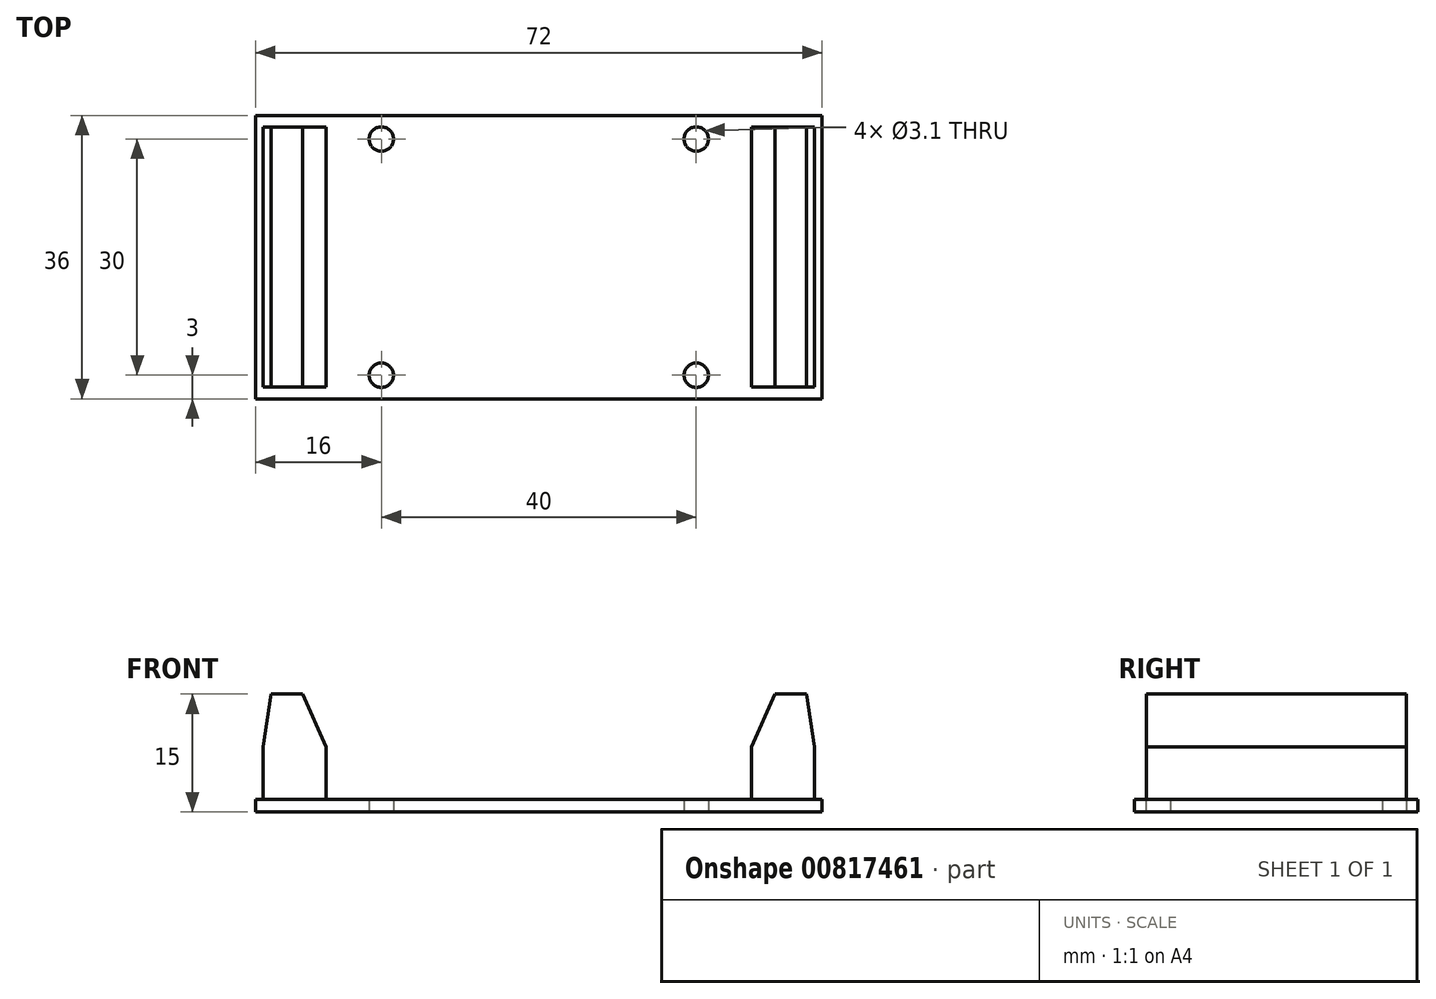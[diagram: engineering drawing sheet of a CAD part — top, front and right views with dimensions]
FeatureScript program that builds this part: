
annotation { "Feature Type Name" : "Feature", "Feature Type Description" : "" }
export const myFeature = defineFeature(function(context is Context, id is Id, definition is map)
    precondition{}
    {
        {
            var Q0;
            Q0=qCreatedBy(makeId("Top.planeOp"),FACE);
            var sketch = newSketch(context, id + "F0", { "sketchPlane" : qUnion([Q0])});
            skLineSegment(sketch, "E0.bottom", {"start": v(36, 18) * mm, "end": v(-36, 18) * mm});
            skLineSegment(sketch, "E0.top", {"start": v(36, -18) * mm, "end": v(-36, -18) * mm});
            skLineSegment(sketch, "E0.left", {"start": v(36, 18) * mm, "end": v(36, -18) * mm});
            skLineSegment(sketch, "E0.right", {"start": v(-36, 18) * mm, "end": v(-36, -18) * mm});
            skPoint(sketch, "E0.middle", {"position": v(0, 0) * mm});
            skLineSegment(sketch, "E1.bottom", {"start": v(20, 15) * mm, "end": v(-20, 15) * mm, "construction": true});
            skLineSegment(sketch, "E1.top", {"start": v(20, -15) * mm, "end": v(-20, -15) * mm, "construction": true});
            skLineSegment(sketch, "E1.left", {"start": v(20, 15) * mm, "end": v(20, -15) * mm, "construction": true});
            skLineSegment(sketch, "E1.right", {"start": v(-20, 15) * mm, "end": v(-20, -15) * mm, "construction": true});
            skCircle(sketch, "E2", {"center": v(-20, 15) * mm, "radius": 1.55 * mm});
            skCircle(sketch, "E3", {"center": v(20, 15) * mm, "radius": 1.55 * mm});
            skCircle(sketch, "E4", {"center": v(20, -15) * mm, "radius": 1.55 * mm});
            skCircle(sketch, "E5", {"center": v(-20, -15) * mm, "radius": 1.55 * mm});
            skSolve(sketch);
        }
        {
            var Q0;
            Q0=makeQuery(id+"F0.imprint","IMPRINT",FACE,{"disambiguationData":[TD([[makeQuery(id+"F0.imprint","IMPRINT",EDGE,{"derivedFrom":sQuery(id+"F0.wireOp",EDGE,"E0.bottom")}),1.0]])]});
            extrude(context, id + "F1", {"entities" : qUnion([Q0]), "depth" : 1.6 * mm, "offsetDistance" : 25 * mm});
        }
        {
            var Q0;
            Q0=qCreatedBy(makeId("Front.planeOp"),FACE);
            var sketch = newSketch(context, id + "F2", { "sketchPlane" : qUnion([Q0])});
            skLineSegment(sketch, "E6.0", {"start": v(36, 1.6) * mm, "end": v(-36, 1.6) * mm});
            skLineSegment(sketch, "E7", {"start": v(-35, 1.6) * mm, "end": v(-35, 8.3) * mm});
            skLineSegment(sketch, "E8", {"start": v(-35, 8.3) * mm, "end": v(-34, 15) * mm});
            skLineSegment(sketch, "E9", {"start": v(-34, 15) * mm, "end": v(-30, 15) * mm});
            skLineSegment(sketch, "E10", {"start": v(-30, 15) * mm, "end": v(-27, 8.3) * mm});
            skLineSegment(sketch, "E11", {"start": v(-27, 8.3) * mm, "end": v(-27, 1.6) * mm});
            skLineSegment(sketch, "E12.MirrorCS", {"start": v(27, 8.3) * mm, "end": v(27, 1.6) * mm});
            skLineSegment(sketch, "E13.MirrorCS", {"start": v(35, 1.6) * mm, "end": v(35, 8.3) * mm});
            skLineSegment(sketch, "E14.MirrorCS", {"start": v(34, 15) * mm, "end": v(30, 15) * mm});
            skLineSegment(sketch, "E15.MirrorCS", {"start": v(30, 15) * mm, "end": v(27, 8.3) * mm});
            skLineSegment(sketch, "E16.MirrorCS", {"start": v(35, 8.3) * mm, "end": v(34, 15) * mm});
            skSolve(sketch);
        }
        {
            var Q0;
            {var subQ0=sQuery(id+"F2.wireOp",EDGE,"E7");Q0=makeQuery(id+"F2.imprint","IMPRINT",FACE,{"disambiguationData":[TD([[makeQuery(id+"F2.imprint","IMPRINT",EDGE,{"derivedFrom":subQ0}),-1.0]])]});}
            var Q1;
            {var subQ1=sQuery(id+"F2.wireOp",EDGE,"E12.MirrorCS");Q1=makeQuery(id+"F2.imprint","IMPRINT",FACE,{"disambiguationData":[TD([[makeQuery(id+"F2.imprint","IMPRINT",EDGE,{"derivedFrom":subQ1}),1.0]])]});}
            extrude(context, id + "F3", {"entities" : qUnion([Q0, Q1]), "operationType" : NewBodyOperationType.ADD, "endBound" : BoundingType.SYMMETRIC, "depth" : 33 * mm, "offsetDistance" : 25 * mm});
        }
    });
